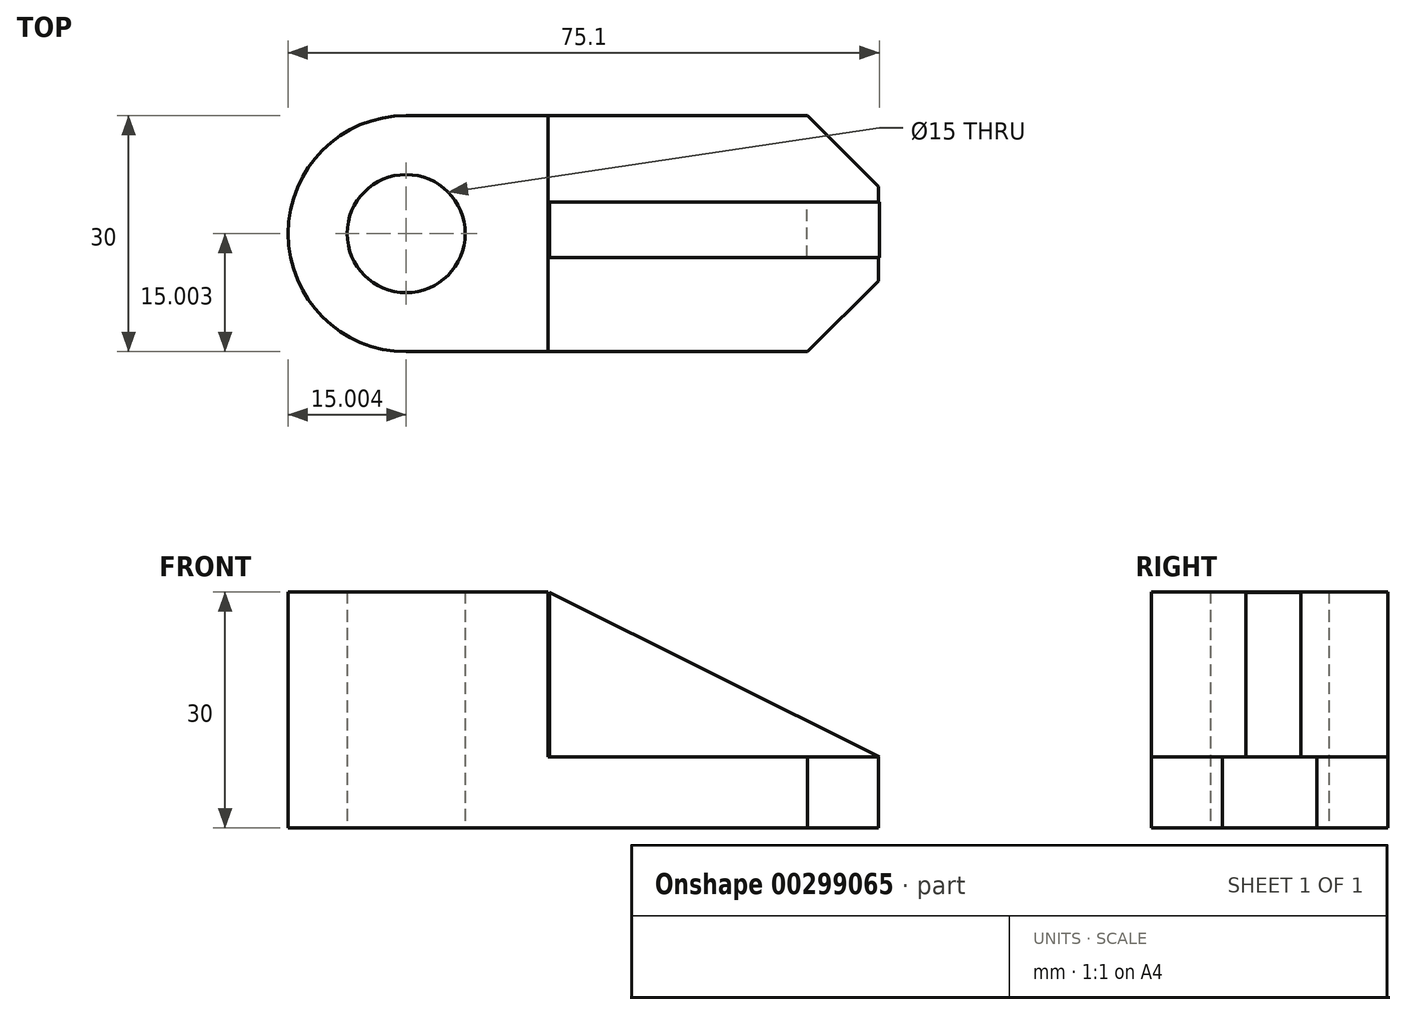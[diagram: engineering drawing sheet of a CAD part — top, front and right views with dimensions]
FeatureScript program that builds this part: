
annotation { "Feature Type Name" : "Feature", "Feature Type Description" : "" }
export const myFeature = defineFeature(function(context is Context, id is Id, definition is map)
    precondition{}
    {
        {
            var Q0;
            Q0=qCreatedBy(makeId("Top.planeOp"),FACE);
            var sketch = newSketch(context, id + "F0", { "sketchPlane" : qUnion([Q0])});
            skArc(sketch, "E0", {"start": v(-36.32, 29.51) * mm, "mid": v(-51.32, 14.51) * mm, "end": v(-36.32, -0.49) * mm});
            skLineSegment(sketch, "E1", {"start": v(-36.32, 29.51) * mm, "end": v(-18.32, 29.51) * mm});
            skLineSegment(sketch, "E2", {"start": v(-18.32, 29.51) * mm, "end": v(-18.32, 18.01) * mm});
            skLineSegment(sketch, "E3", {"start": v(-18.32, -0.49) * mm, "end": v(-36.32, -0.49) * mm});
            skCircle(sketch, "E4", {"center": v(-36.32, 14.51) * mm, "radius": 7.5 * mm});
            skLineSegment(sketch, "E5", {"start": v(-18.32, 29.51) * mm, "end": v(14.68, 29.51) * mm});
            skLineSegment(sketch, "E6", {"start": v(14.68, 29.51) * mm, "end": v(23.68, 20.51) * mm});
            skLineSegment(sketch, "E7", {"start": v(23.68, 20.51) * mm, "end": v(23.68, 8.51) * mm});
            skLineSegment(sketch, "E8", {"start": v(23.68, 8.51) * mm, "end": v(14.68, -0.49) * mm});
            skLineSegment(sketch, "E9", {"start": v(14.68, -0.49) * mm, "end": v(-18.32, -0.49) * mm});
            skLineSegment(sketch, "E10", {"start": v(-51.32, 14.51) * mm, "end": v(23.68, 14.51) * mm, "construction": true});
            skLineSegment(sketch, "E11", {"start": v(-18.32, 18.01) * mm, "end": v(23.68, 18.01) * mm});
            skLineSegment(sketch, "E12", {"start": v(-18.32, 11.01) * mm, "end": v(23.68, 11.01) * mm});
            skLineSegment(sketch, "E13.trimOffspring", {"start": v(-18.32, 11.01) * mm, "end": v(-18.32, -0.49) * mm});
            skLineSegment(sketch, "E14", {"start": v(-18.32, 18.01) * mm, "end": v(-18.32, 11.01) * mm});
            skSolve(sketch);
        }
        {
            var Q0;
            {var subQ1=sQuery(id+"F0.wireOp",EDGE,"E8");Q0=makeQuery(id+"F0.imprint","IMPRINT",FACE,{"disambiguationData":[TD([[makeQuery(id+"F0.imprint","IMPRINT",EDGE,{"derivedFrom":subQ1}),-1.0]])]});}
            var Q1;
            Q1=makeQuery(id+"F0.imprint","IMPRINT",FACE,{"disambiguationData":[TD([[makeQuery(id+"F0.imprint","IMPRINT",EDGE,{"derivedFrom":sQuery(id+"F0.wireOp",EDGE,"E2")}),1.0]])]});
            var Q2;
            {var subQ0=sQuery(id+"F0.wireOp",EDGE,"E11");Q2=makeQuery(id+"F0.imprint","IMPRINT",FACE,{"disambiguationData":[TD([[makeQuery(id+"F0.imprint","IMPRINT",EDGE,{"derivedFrom":subQ0}),-1.0]])]});}
            extrude(context, id + "F1", {"entities" : qUnion([Q0, Q1, Q2]), "depth" : 9 * mm});
        }
        {
            var Q0;
            Q0=makeQuery(id+"F0.imprint","IMPRINT",FACE,{"disambiguationData":[TD([[makeQuery(id+"F0.imprint","IMPRINT",EDGE,{"derivedFrom":sQuery(id+"F0.wireOp",EDGE,"E0")}),1.0]])]});
            extrude(context, id + "F2", {"entities" : qUnion([Q0]), "operationType" : NewBodyOperationType.ADD, "depth" : 30 * mm});
        }
        {
            var Q0;
            Q0=qCreatedBy(makeId("Front.planeOp"),FACE);
            var sketch = newSketch(context, id + "F3", { "sketchPlane" : qUnion([Q0])});
            skLineSegment(sketch, "E15.0", {"start": v(-18.1, 29.92) * mm, "end": v(-18.1, 8.92) * mm});
            skLineSegment(sketch, "E16", {"start": v(-18.1, 29.92) * mm, "end": v(23.78, 9.02) * mm});
            skLineSegment(sketch, "E17", {"start": v(-18.1, 8.92) * mm, "end": v(-18.1, 29.92) * mm});
            skLineSegment(sketch, "E18", {"start": v(-18.1, 8.92) * mm, "end": v(23.78, 9.02) * mm});
            skSolve(sketch);
        }
        {
            var Q0;
            Q0=qSketchRegion(id+"F3",true);
            extrude(context, id + "F4", {"entities" : qUnion([Q0]), "operationType" : NewBodyOperationType.ADD, "oppositeDirection" : true, "depth" : 18.5 * mm});
        }
        {
            var Q0;
            Q0=makeQuery(id+"F4.opExtrude","CAP_FACE",FACE,{"disambiguationData":[OSD([sQuery(id+"F3.wireOp",EDGE,"E16"),sQuery(id+"F3.wireOp",EDGE,"E17"),sQuery(id+"F3.wireOp",EDGE,"E18")])],"isStart":true});
            extrude(context, id + "F5", {"entities" : qUnion([Q0]), "operationType" : NewBodyOperationType.REMOVE, "oppositeDirection" : true, "depth" : 11.5 * mm});
        }
    });
